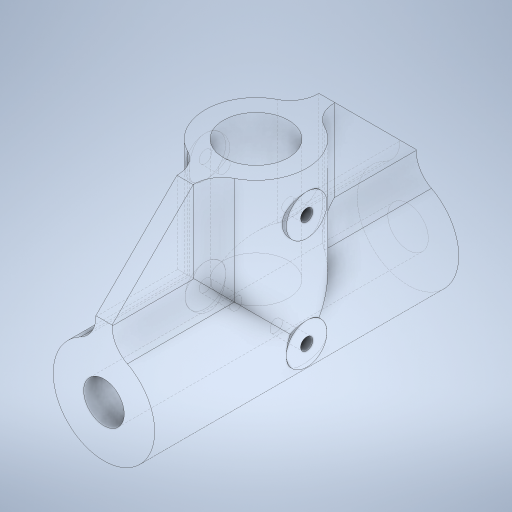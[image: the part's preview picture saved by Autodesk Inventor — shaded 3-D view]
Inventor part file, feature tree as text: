
AUTODESK INVENTOR PART (.ipt)
format: ipt  version: 2023 (Build 270158000, 158)  size: 388,608 bytes
history: native  units: in
note: dims shown in document units (in); Inventor stores cm internally (conversion verified against a paired STEP export)
features: extrude x6, sketch x6, chamfer x1, fillet x1, plane x1
ambient origin geometry x8: Origin, YZ Plane, XZ Plane, XY Plane, X Axis, Y Axis, Z Axis, Center Point
bodies: Solid1 (feature_tree)
feature tree (15):
  extrude  "Extrusion1"  Depth=2.9528in TaperAngle=0.0deg
  extrude  "Extrusion4"  Depth=0.9843in
  chamfer  "Chamfer1"  Distance=0.3937in
  fillet  "Fillet1"  Radius=0.6299in
  plane  "Work Plane2"
  sketch  "Sketch8"  dims[d21=1.1811in d22=0.0in d23=0.7874in d24=0.0787in d25=45.0deg]
  extrude  "Extrusion6"  Depth=0.7874in TaperAngle=45.0deg
  extrude  "Extrusion5"  Depth=0.3937in
  extrude  "Extrusion3"  Depth=0.3937in
  extrude  "Extrusion7"  Depth=0.3937in
  sketch  "Sketch1"  dims[d1=0.9843in d2=2.9528in d3=0.0in]
  sketch  "Sketch4"  dims[d12=0.9843in d13=0.0in d14=0.9843in]
  sketch  "Sketch5"  dims[d15=0.0787in]
  sketch  "Sketch6"  dims[d16=0.0787in d18=0.3937in d19=0.0in d20=0.6299in]
  sketch  "Sketch9"  dims[d26=0.2756in d30=0.3937in d31=0.3937in d32=0.3937in d33=0.3937in d34=0.9843in d35=0.0in d36=0.1181in d37=0.1181in d38=0.9843in d39=0.0in]
